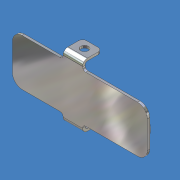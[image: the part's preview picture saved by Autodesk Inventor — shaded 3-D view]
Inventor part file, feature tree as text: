
AUTODESK INVENTOR PART (.ipt)
format: ipt  version: unknown  size: 293,888 bytes
history: native  units: mm (DEFAULTED — no unit token found)
features: sheet_metal_op x9, sketch x7, other x5, chamfer x3, hole x1, extrude x1
ambient origin geometry x8: Origin, YZ Plane, XZ Plane, XY Plane, X Axis, Y Axis, Z Axis, Center Point
feature tree (26):
  sheet_metal_op  "Face1"
  sheet_metal_op  "Face2"
  sheet_metal_op  "Face3"
  chamfer  "Corner Round3"
  sheet_metal_op  "Flange1"
  sheet_metal_op  "Flange2"
  chamfer  "Corner Round2"
  chamfer  "Corner Round1"
  hole  "Hole1"  [1 undecoded]
  extrude  "Extrusion1"  Depth=3.175mm
  sketch  "Sketch1"  dims[d0=15.24mm d1=43.942mm]
  other  "Plate1"
  sketch  "Sketch2"  dims[d2=0.7874mm d3=3.175mm]
  other  "Plate2"
  sheet_metal_op  "Bend1"
  sketch  "Sketch3"  dims[d4=6.35mm]
  other  "Plate3"
  sheet_metal_op  "Bend2"
  sketch  "Sketch4"  dims[d5=2.6924mm]
  other  "Plate4"
  sheet_metal_op  "Bend3"
  sketch  "Sketch5"  dims[d6=16.51mm]
  other  "Plate5"
  sheet_metal_op  "Bend4"
  sketch  "Sketch6"  dims[d7=0.7874mm]
  sketch  "Sketch8"  dims[d8=0.7874mm d9=0.3937mm d10=1.5748mm d11=0.7874mm d12=0.7874mm d13=0.3937mm d14=1.5748mm d15=0.7874mm d16=6.35mm d17=90.0deg d18=0.7874mm d19=1.27mm d20=1.016mm d21=0.7874mm d22=0.7874mm d23=0.3937mm d24=1.5748mm d25=0.7874mm d26=0.7874mm d27=0.3937mm d28=1.5748mm d29=0.7874mm d30=6.604mm d31=90.0deg d32=0.7874mm d33=2.54mm d34=2.54mm d35=12.7mm d36=9.525mm d37=6.35mm d38=14.3117mm d39=19.05mm d40=20.594885mm d44=8.0mm d45=1.27mm d46=0.0mm d47=19.304mm]
note: 1 required parameter value undecoded (feature->parameter linkage not recoverable at this tier; creation-order binding heuristic only, values carry confidence <= 0.55)
